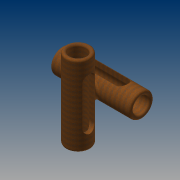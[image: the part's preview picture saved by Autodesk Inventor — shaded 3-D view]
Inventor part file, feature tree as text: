
AUTODESK INVENTOR PART (.ipt)
format: ipt  version: 2015 (Build 190159000, 159)  size: 284,672 bytes
history: native  units: mm
features: extrude x5, sketch x5, fillet x3, plane x3
ambient origin geometry x8: Origin, YZ Plane, XZ Plane, XY Plane, X Axis, Y Axis, Z Axis, Center Point
bodies: Solid1 (feature_tree)
feature tree (16):
  extrude  "Extrusion1"  Depth=40.0mm
  fillet  "Fillet1"  Radius=200.0mm
  plane  "Work Plane1"
  extrude  "Extrusion2"  Depth=30.0mm
  plane  "Work Plane2"
  extrude  "Extrusion3"  Depth=15.0mm
  extrude  "Extrusion4"  Depth=150.0mm TaperAngle=0.0deg
  fillet  "Fillet2"  Radius=30.0mm
  plane  "Work Plane3"
  extrude  "Extrusion5"  Depth=100.0mm
  fillet  "Fillet3"  Radius=10.0mm
  sketch  "Sketch1"  dims[d0=60.0mm d1=40.0mm d2=200.0mm d3=0.0mm]
  sketch  "Sketch2"  dims[d4=5.0mm d5=30.0mm]
  sketch  "Sketch3"  dims[d6=100.0mm d7=15.0mm]
  sketch  "Sketch4"  dims[d8=100.0mm d9=150.0mm d10=0.0mm d11=30.0mm]
  sketch  "Sketch5"  dims[d12=40.0mm d13=100.0mm d14=10.0mm d15=0.0mm d16=10.0mm d17=0.0mm d18=60.0mm d19=40.0mm d21=30.0mm d22=200.0mm d23=0.0mm d24=5.0mm d25=100.0mm d26=100.0mm d27=15.0mm d28=30.0mm d29=100.0mm d30=200.0mm d31=0.0mm d32=5.0mm]
